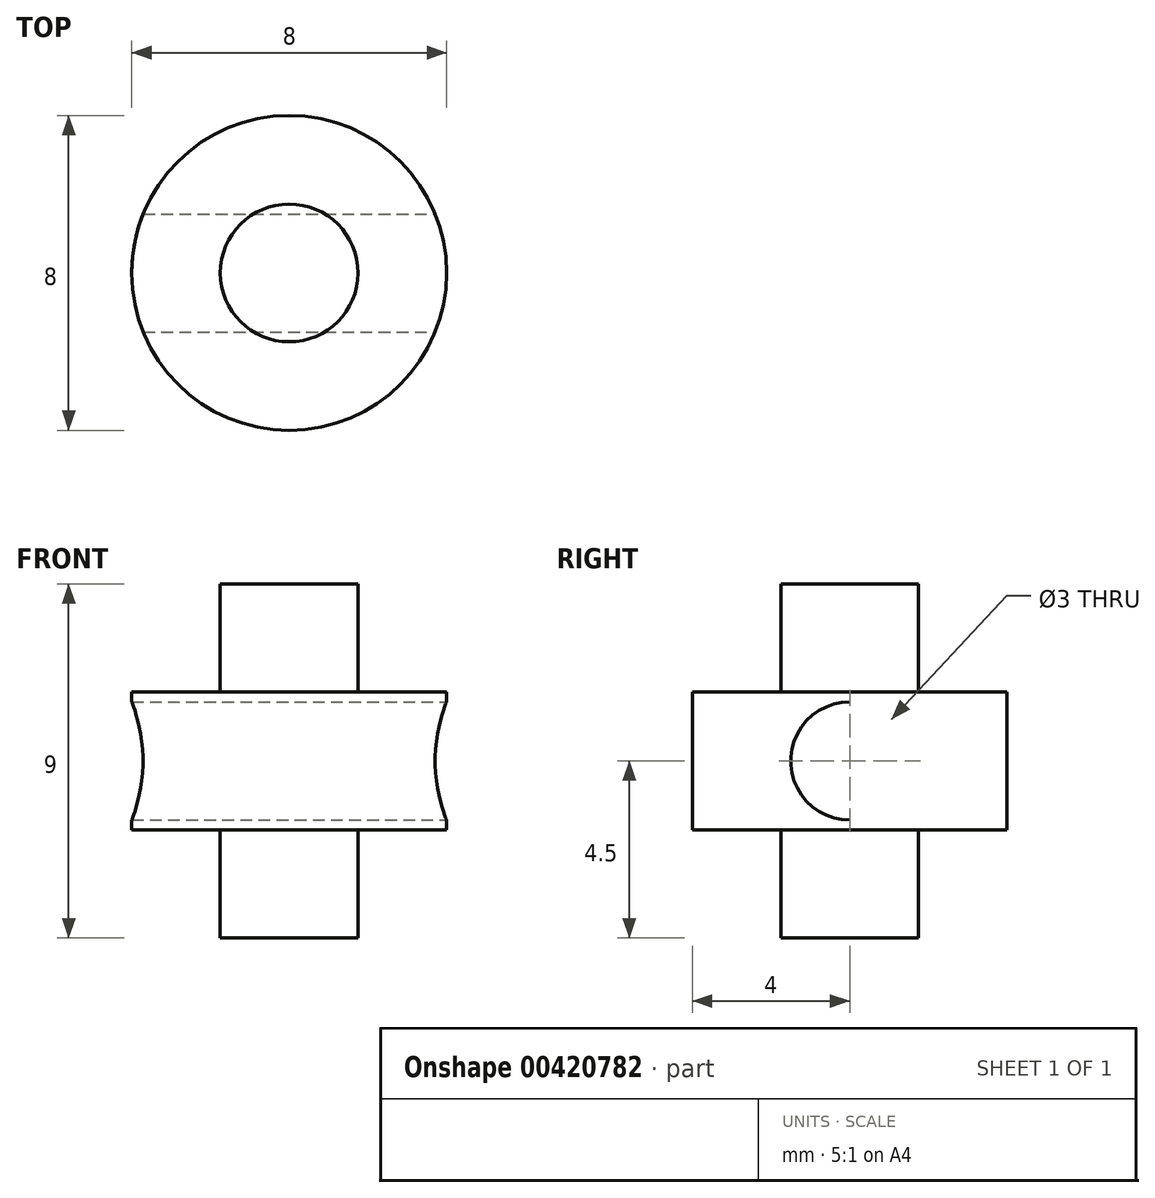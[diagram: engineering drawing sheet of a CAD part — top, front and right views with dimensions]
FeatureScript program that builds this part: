
annotation { "Feature Type Name" : "Feature", "Feature Type Description" : "" }
export const myFeature = defineFeature(function(context is Context, id is Id, definition is map)
    precondition{}
    {
        {
            var Q0;
            Q0=qCreatedBy(makeId("Top.planeOp"),FACE);
            var sketch = newSketch(context, id + "F0", { "sketchPlane" : qUnion([Q0])});
            skCircle(sketch, "E0", {"center": v(0, 0) * mm, "radius": 4 * mm});
            skCircle(sketch, "E1", {"center": v(0, 0) * mm, "radius": 1.75 * mm});
            skSolve(sketch);
        }
        {
            var Q0;
            Q0=makeQuery(id+"F0.imprint","IMPRINT",FACE,{"disambiguationData":[TD([[makeQuery(id+"F0.imprint","IMPRINT",EDGE,{"derivedFrom":sQuery(id+"F0.wireOp",EDGE,"E0")}),1.0]])]});
            var Q1;
            Q1=sQuery(id+"F0.wireOp",EDGE,"E0");
            extrude(context, id + "F1", {"entities" : qUnion([Q0]), "surfaceEntities" : qUnion([Q1]), "endBound" : BoundingType.SYMMETRIC, "depth" : 3.5 * mm});
        }
        {
            var Q0;
            Q0=makeQuery(id+"F0.imprint","IMPRINT",FACE,{"disambiguationData":[TD([[makeQuery(id+"F0.imprint","IMPRINT",EDGE,{"derivedFrom":sQuery(id+"F0.wireOp",EDGE,"E1")}),1.0]])]});
            extrude(context, id + "F2", {"entities" : qUnion([Q0]), "operationType" : NewBodyOperationType.ADD, "endBound" : BoundingType.SYMMETRIC, "depth" : 9 * mm});
        }
        {
            var Q0;
            Q0=qCreatedBy(makeId("Right.planeOp"),FACE);
            var sketch = newSketch(context, id + "F3", { "sketchPlane" : qUnion([Q0])});
            skCircle(sketch, "E2", {"center": v(0, 0) * mm, "radius": 1.5 * mm});
            skSolve(sketch);
        }
        {
            var Q0;
            Q0 = qSketchRegion(id + "F3", true);
            extrude(context, id + "F4", {"entities" : qUnion([Q0]), "operationType" : NewBodyOperationType.REMOVE, "endBound" : BoundingType.SYMMETRIC, "oppositeDirection" : true, "depth" : 10 * mm});
        }
    });
